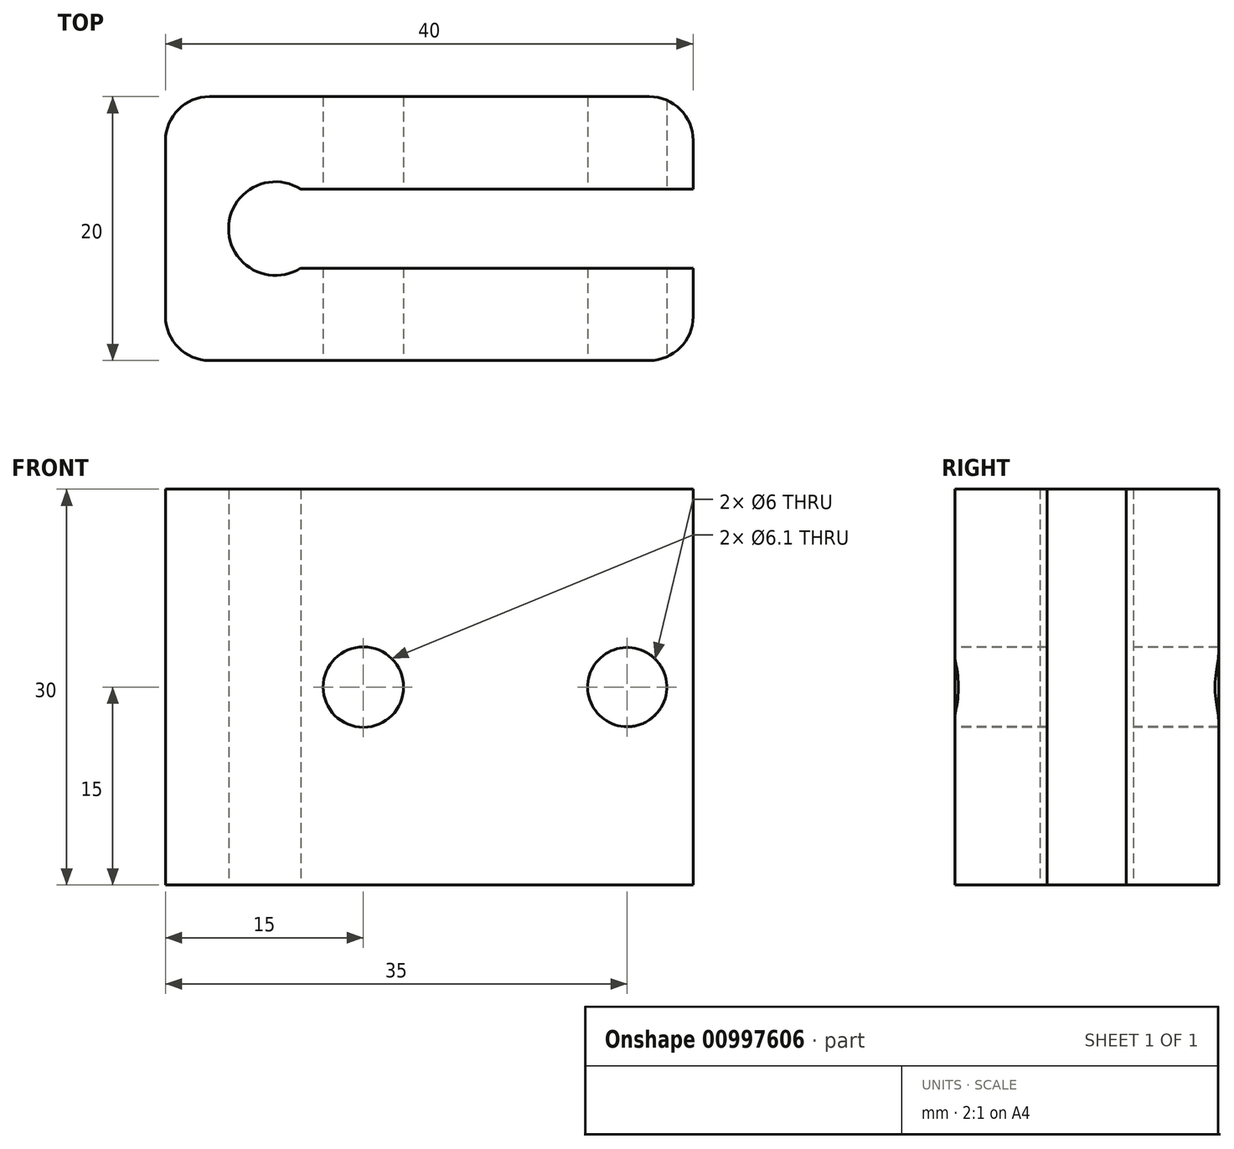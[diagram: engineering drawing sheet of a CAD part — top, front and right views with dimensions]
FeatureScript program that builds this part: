
annotation { "Feature Type Name" : "Feature", "Feature Type Description" : "" }
export const myFeature = defineFeature(function(context is Context, id is Id, definition is map)
    precondition{}
    {
        {
            var Q0;
            Q0=qCreatedBy(makeId("Top.planeOp"),FACE);
            var sketch = newSketch(context, id + "F0", { "sketchPlane" : qUnion([Q0])});
            skLineSegment(sketch, "E0.right", {"start": v(-20, -6.67) * mm, "end": v(-20, 6.67) * mm});
            skPoint(sketch, "E0.middle", {"position": v(0, 0) * mm});
            skLineSegment(sketch, "E1", {"start": v(20, 6.67) * mm, "end": v(20, 3) * mm});
            skLineSegment(sketch, "E2", {"start": v(20, -3) * mm, "end": v(20, -6.67) * mm});
            skPoint(sketch, "E3.visualSharp", {"position": v(-20, 10) * mm});
            skArc(sketch, "E3.filletArc", {"start": v(-16.67, 10) * mm, "mid": v(-19.02, 9.02) * mm, "end": v(-20, 6.67) * mm});
            skPoint(sketch, "E4.visualSharp", {"position": v(-20, -10) * mm});
            skArc(sketch, "E4.filletArc", {"start": v(-20, -6.67) * mm, "mid": v(-19.02, -9.02) * mm, "end": v(-16.67, -10) * mm});
            skPoint(sketch, "E5.visualSharp", {"position": v(20, 10) * mm});
            skArc(sketch, "E5.filletArc", {"start": v(20, 6.67) * mm, "mid": v(19.02, 9.02) * mm, "end": v(16.67, 10) * mm});
            skPoint(sketch, "E6.visualSharp", {"position": v(20, -10) * mm});
            skArc(sketch, "E6.filletArc", {"start": v(16.67, -10) * mm, "mid": v(19.02, -9.02) * mm, "end": v(20, -6.67) * mm});
            skLineSegment(sketch, "E7", {"start": v(-16.67, -10) * mm, "end": v(16.67, -10) * mm});
            skLineSegment(sketch, "E8", {"start": v(-16.67, 10) * mm, "end": v(16.67, 10) * mm});
            skLineSegment(sketch, "E9", {"start": v(20, 3) * mm, "end": v(-9.76, 3) * mm});
            skLineSegment(sketch, "E10", {"start": v(20, -3) * mm, "end": v(-9.76, -3) * mm});
            skLineSegment(sketch, "E11", {"start": v(-9.76, 3) * mm, "end": v(-9.76, -3) * mm});
            skCircle(sketch, "E12", {"center": v(-11.67, 0) * mm, "radius": 3.55 * mm});
            skSolve(sketch);
        }
        {
            var Q0;
            Q0=makeQuery(id+"F0.imprint","IMPRINT",FACE,{"disambiguationData":[TD([[makeQuery(id+"F0.imprint","IMPRINT",EDGE,{"derivedFrom":sQuery(id+"F0.wireOp",EDGE,"E0.right")}),-1.0]])]});
            extrude(context, id + "F1", {"entities" : qUnion([Q0]), "depth" : 30 * mm, "offsetDistance" : 25 * mm});
        }
        {
            var Q0;
            Q0=makeQuery(id+"F1.opExtrude","SWEPT_FACE",FACE,{"disambiguationData":[OSD([sQuery(id+"F0.wireOp",EDGE,"E7")])]});
            var sketch = newSketch(context, id + "F2", { "sketchPlane" : qUnion([Q0])});
            skCircle(sketch, "E13", {"center": v(-5, 15) * mm, "radius": 3.05 * mm});
            skCircle(sketch, "E14", {"center": v(15, 15) * mm, "radius": 3 * mm});
            skSolve(sketch);
        }
        {
            var Q0;
            Q0=makeQuery(id+"F2.imprint","IMPRINT",FACE,{"disambiguationData":[TD([[makeQuery(id+"F2.imprint","IMPRINT",EDGE,{"derivedFrom":sQuery(id+"F2.wireOp",EDGE,"E13")}),1.0]])]});
            var Q1;
            Q1=makeQuery(id+"F2.imprint","IMPRINT",FACE,{"disambiguationData":[TD([[makeQuery(id+"F2.imprint","IMPRINT",EDGE,{"derivedFrom":sQuery(id+"F2.wireOp",EDGE,"E14")}),1.0]])]});
            extrude(context, id + "F3", {"entities" : qUnion([Q0, Q1]), "operationType" : NewBodyOperationType.REMOVE, "oppositeDirection" : true, "depth" : 30 * mm, "offsetDistance" : 25 * mm});
        }
    });
